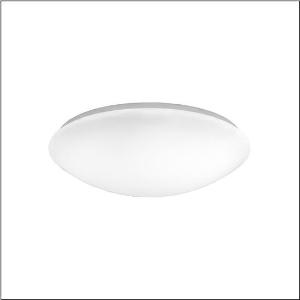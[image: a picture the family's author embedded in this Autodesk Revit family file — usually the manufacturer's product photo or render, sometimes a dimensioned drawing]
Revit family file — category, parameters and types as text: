
# Revit family: round_31_b_5pja232001a
name_source: partatom
category: Lighting Fixtures
units: mm (PartAtom-declared; Revit-internal decimal feet)

## family parameters
Cut with Voids When Loaded = No
Host = Face
Light Source = No
Part Type = Normal
Room Calculation Point = No
Round Connector Dimension = Use Diameter
Shared = No

## types (1)
- --- (1 x LED, 4900 lm, 39 W, 4000K)
    Apparent Load = 39 VA
    CIE Flux Codes = 42 71 89 88 100
    Color Rendering = 80
    Color Temperature = 4000K
    Default Elevation = 1800 mm
    Description = Round 31 B, wall and ceiling luminaire, primary optical cover: enclosure, of PMMA, light emission: direct distribution, primary light characteristic: symmetric, installation type: surface-mounted, LED, rated luminous flux: 4.900lm, luminous efficacy: 126lm/W, light colour: 840, colour temperature: 4000K, with terminal, 3+2-pole, max. 2.5mm², mains connection: 230V, AC, 50/60Hz, rated input power: 39W, luminaire housing, round, of steel, white, diameter: 464mm, height: 120mm, protection rating (complete): IP40, insulation class (complete): insulation class I (protective earthing), certification: CE, impact resistance: IK02, packaging unit: 1 piece
    Height = 120 mm
    Lamp = 1 x LED
    Lamp Light Flux = 4900 lm
    Lamp Power = 39 W
    Lamp count = 1
    Length = 464 mm
    Luminous efficacy = 126 lm/W
    Manufacturer = Siteco
    ModVariant = No
    Model = 5PJA232001A
    Mounting Place = Ceiling
    Mounting Type = Surface mounted
    Number of Poles = 1
    OnlyDefault = Yes
    Power Factor = 1
    Product Name = Round 31 B
    Product group = wall and ceiling luminaire
    ProductGroupID = 301
    Protection Class = Protection class I
    Protection Degree = IP 40
    RLX_Detail_Level = 1
    RLX_Emergency_Light_Flux = 0 lm
    RLX_Emergency_Type = 0
    RLX_Emergency_Type_DB = No
    RlxData = <blob elided: 13745 chars, md5=13b5164b>
    Socket = socket
    Standby Power = 0 W
    System Light Flux = 4900 lm
    System Power = 39 W
    Type Comments = factory setting: luminous flux: 100 % | (ON | ON | ON) | 1050 mA
    Type Image = l_1258313.jpg
    URL = http://relux.com
    VarID = @adj_013657
    Voltage = 0 V
    Weight = 0.00 kg
    Width = 0 mm  [stored 0 ft]

note: [stored X ft] marks values corroborated as IEEE doubles in the binary element streams (Revit-internal decimal feet)

## geometry (parser evidence)
native form markers: Sweep x11
no freeform markers — native parametric forms only
